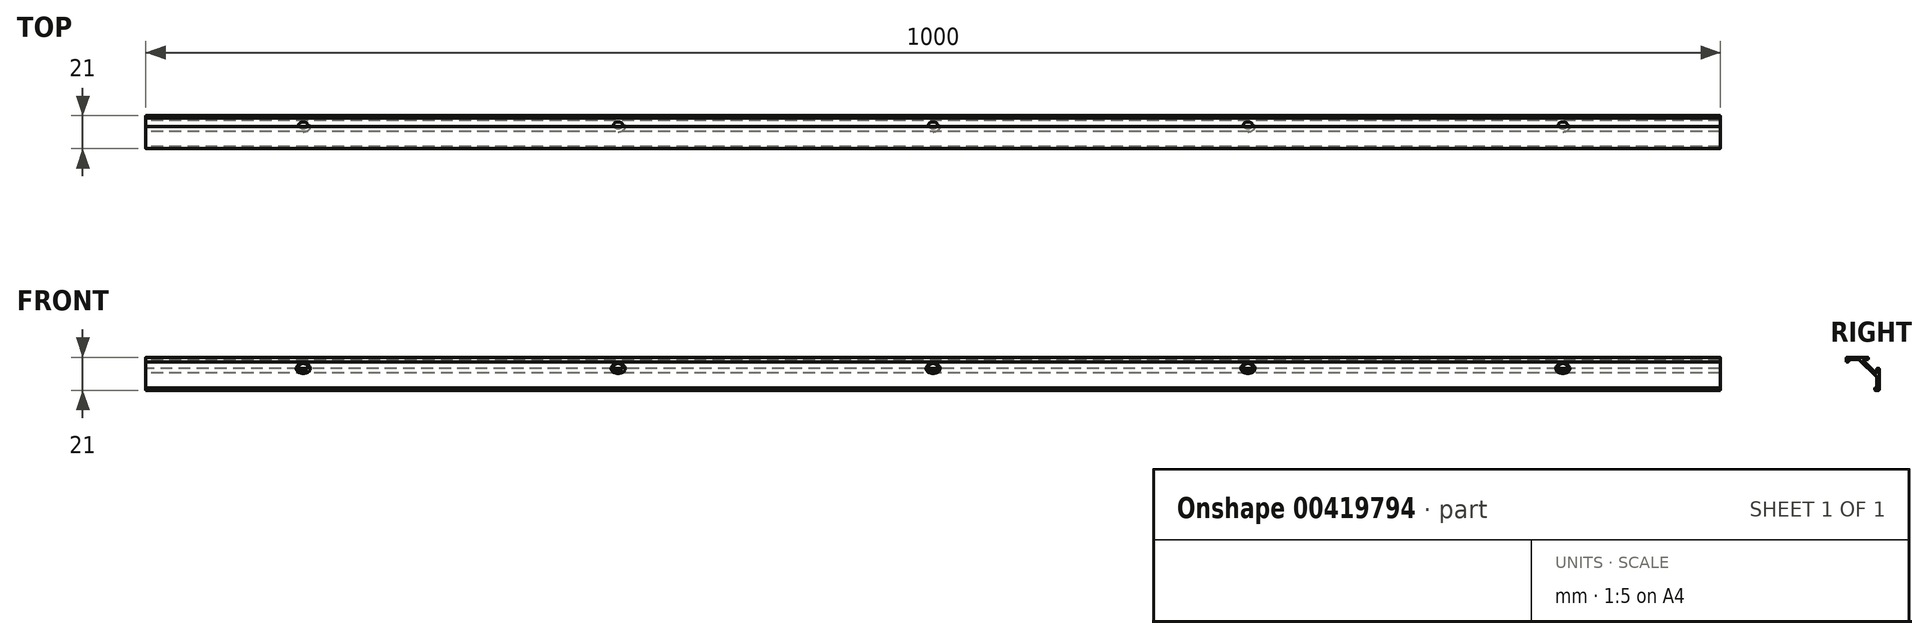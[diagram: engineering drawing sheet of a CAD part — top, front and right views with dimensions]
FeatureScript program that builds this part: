
annotation { "Feature Type Name" : "Feature", "Feature Type Description" : "" }
export const myFeature = defineFeature(function(context is Context, id is Id, definition is map)
    precondition{}
    {
        {
            var Q0;
            Q0=qCreatedBy(makeId("Right.planeOp"),FACE);
            var sketch = newSketch(context, id + "F0", { "sketchPlane" : qUnion([Q0])});
            skLineSegment(sketch, "E0.bottom", {"start": v(10, -10.5) * mm, "end": v(8, -10.5) * mm});
            skLineSegment(sketch, "E0.top", {"start": v(3, 10.5) * mm, "end": v(-10, 10.5) * mm});
            skLineSegment(sketch, "E0.left", {"start": v(10.5, -10) * mm, "end": v(10.5, 3) * mm});
            skLineSegment(sketch, "E0.right", {"start": v(-10.5, 8) * mm, "end": v(-10.5, 10) * mm});
            skPoint(sketch, "E0.middle", {"position": v(0, 0) * mm});
            skLineSegment(sketch, "E1.0", {"start": v(-9, 8) * mm, "end": v(-9, 8.5) * mm});
            skLineSegment(sketch, "E2.0", {"start": v(8.5, -9) * mm, "end": v(8, -9) * mm});
            skLineSegment(sketch, "E3.0", {"start": v(3.5, 9.5) * mm, "end": v(3.5, 10) * mm, "construction": true});
            skLineSegment(sketch, "E4.0", {"start": v(10, 3.5) * mm, "end": v(9.5, 3.5) * mm, "construction": true});
            skLineSegment(sketch, "E5.trimOffspring", {"start": v(-9.5, 7.5) * mm, "end": v(-10, 7.5) * mm});
            skLineSegment(sketch, "E6.0", {"start": v(7.5, -10) * mm, "end": v(7.5, -9.5) * mm});
            skPoint(sketch, "E7.orphan", {"position": v(-10.5, -10.5) * mm});
            skArc(sketch, "E8.filletArc", {"start": v(-8.5, 9) * mm, "mid": v(-8.85, 8.85) * mm, "end": v(-9, 8.5) * mm});
            skArc(sketch, "E9.filletArc", {"start": v(-9.5, 7.5) * mm, "mid": v(-9.15, 7.65) * mm, "end": v(-9, 8) * mm});
            skPoint(sketch, "E10.visualSharp", {"position": v(-10.5, 7.5) * mm});
            skArc(sketch, "E10.filletArc", {"start": v(-10.5, 8) * mm, "mid": v(-10.35, 7.65) * mm, "end": v(-10, 7.5) * mm});
            skArc(sketch, "E11.filletArc", {"start": v(-10, 10.5) * mm, "mid": v(-10.35, 10.35) * mm, "end": v(-10.5, 10) * mm});
            skPoint(sketch, "E12.visualSharp", {"position": v(7.5, -9) * mm});
            skArc(sketch, "E12.filletArc", {"start": v(8, -9) * mm, "mid": v(7.65, -9.15) * mm, "end": v(7.5, -9.5) * mm});
            skPoint(sketch, "E13.visualSharp", {"position": v(7.5, -10.5) * mm});
            skArc(sketch, "E13.filletArc", {"start": v(7.5, -10) * mm, "mid": v(7.65, -10.35) * mm, "end": v(8, -10.5) * mm});
            skPoint(sketch, "E14.visualSharp", {"position": v(10.5, -10.5) * mm});
            skArc(sketch, "E14.filletArc", {"start": v(10, -10.5) * mm, "mid": v(10.35, -10.35) * mm, "end": v(10.5, -10) * mm});
            skArc(sketch, "E15.filletArc", {"start": v(8.5, -9) * mm, "mid": v(8.85, -8.85) * mm, "end": v(9, -8.5) * mm});
            skLineSegment(sketch, "E16.trimOffspring", {"start": v(-2.52, 9) * mm, "end": v(-8.5, 9) * mm});
            skLineSegment(sketch, "E17.trimOffspring", {"start": v(9, -2.52) * mm, "end": v(9, -8.5) * mm});
            skArc(sketch, "E18.filletArc", {"start": v(8.15, 0.66) * mm, "mid": v(8.7, 0.55) * mm, "end": v(9, 1.01) * mm});
            skArc(sketch, "E19.filletArc", {"start": v(1.01, 9) * mm, "mid": v(0.55, 8.7) * mm, "end": v(0.66, 8.15) * mm});
            skArc(sketch, "E20.filletArc", {"start": v(9, -2.52) * mm, "mid": v(8.96, -2.33) * mm, "end": v(8.85, -2.17) * mm});
            skArc(sketch, "E21.filletArc", {"start": v(-2.17, 8.85) * mm, "mid": v(-2.33, 8.96) * mm, "end": v(-2.52, 9) * mm});
            skLineSegment(sketch, "E22", {"start": v(3.5, 10) * mm, "end": v(3.5, 9.5) * mm});
            skLineSegment(sketch, "E23", {"start": v(10, 3.5) * mm, "end": v(9.5, 3.5) * mm});
            skArc(sketch, "E24.filletArc", {"start": v(3, 9) * mm, "mid": v(3.35, 9.15) * mm, "end": v(3.5, 9.5) * mm});
            skArc(sketch, "E25.filletArc", {"start": v(3.5, 10) * mm, "mid": v(3.35, 10.35) * mm, "end": v(3, 10.5) * mm});
            skArc(sketch, "E26.filletArc", {"start": v(9.5, 3.5) * mm, "mid": v(9.15, 3.35) * mm, "end": v(9, 3) * mm});
            skArc(sketch, "E27.filletArc", {"start": v(10.5, 3) * mm, "mid": v(10.35, 3.35) * mm, "end": v(10, 3.5) * mm});
            skLineSegment(sketch, "E28", {"start": v(7.5, -10.5) * mm, "end": v(-10.5, 7.5) * mm, "construction": true});
            skLineSegment(sketch, "E29", {"start": v(0.66, 8.15) * mm, "end": v(8.15, 0.66) * mm});
            skLineSegment(sketch, "E30", {"start": v(8.85, -2.17) * mm, "end": v(-2.17, 8.85) * mm});
            skLineSegment(sketch, "E31", {"start": v(9, 3) * mm, "end": v(9, 1.01) * mm});
            skLineSegment(sketch, "E32", {"start": v(3, 9) * mm, "end": v(1.01, 9) * mm});
            skSolve(sketch);
        }
        {
            var Q0;
            Q0=makeQuery(id+"F0.imprint","IMPRINT",FACE,{"disambiguationData":[TD([[makeQuery(id+"F0.imprint","IMPRINT",EDGE,{"derivedFrom":sQuery(id+"F0.wireOp",EDGE,"E0.bottom")}),-1.0]])]});
            extrude(context, id + "F1", {"entities" : qUnion([Q0]), "depth" : 1000 * mm});
        }
        {
            var Q0;
            Q0=makeQuery(id+"F1.opExtrude","SWEPT_FACE",FACE,{"disambiguationData":[OSD([sQuery(id+"F0.wireOp",EDGE,"E30")])]});
            var sketch = newSketch(context, id + "F2", { "sketchPlane" : qUnion([Q0])});
            skLineSegment(sketch, "E33", {"start": v(0, 0) * mm, "end": v(250, 0) * mm});
            skLineSegment(sketch, "E34.0", {"start": v(900, 4.8) * mm, "end": v(900, -4.8) * mm, "construction": true});
            skLineSegment(sketch, "E35.0", {"start": v(700, 4.8) * mm, "end": v(700, -4.8) * mm, "construction": true});
            skLineSegment(sketch, "E36.0", {"start": v(500, 4.8) * mm, "end": v(500, -4.8) * mm, "construction": true});
            skLineSegment(sketch, "E37.0", {"start": v(300, 4.8) * mm, "end": v(300, -4.8) * mm, "construction": true});
            skPoint(sketch, "E38", {"position": v(300, 0) * mm});
            skPoint(sketch, "E39", {"position": v(500, 0) * mm});
            skPoint(sketch, "E40", {"position": v(700, 0) * mm});
            skPoint(sketch, "E41", {"position": v(900, 0) * mm});
            skLineSegment(sketch, "E42.0", {"start": v(100, 4.8) * mm, "end": v(100, -4.8) * mm});
            skPoint(sketch, "E43", {"position": v(100, 0) * mm});
            skSolve(sketch);
        }
        {
            var Q0;
            Q0=sQuery(id+"F2.wireOp",VERTEX,"E38");
            var Q1;
            Q1=sQuery(id+"F2.wireOp",VERTEX,"E39");
            var Q2;
            Q2=sQuery(id+"F2.wireOp",VERTEX,"E40");
            var Q3;
            Q3=sQuery(id+"F2.wireOp",VERTEX,"E41");
            var Q4;
            Q4=sQuery(id+"F2.wireOp",VERTEX,"E43");
            var Q5;
            Q5=makeQuery(id+"F1.opExtrude","SWEPT_BODY",BODY,{"disambiguationData":[OSD([sQuery(id+"F0.wireOp",EDGE,"E0.bottom"),sQuery(id+"F0.wireOp",EDGE,"E0.top"),sQuery(id+"F0.wireOp",EDGE,"E0.left"),sQuery(id+"F0.wireOp",EDGE,"E0.right"),sQuery(id+"F0.wireOp",EDGE,"E1.0"),sQuery(id+"F0.wireOp",EDGE,"E2.0"),sQuery(id+"F0.wireOp",EDGE,"s1j5iu09-LJZy-9apo-odkQ-GbOXyxKkjL7w"),sQuery(id+"F0.wireOp",EDGE,"fCwWEJ1m-8jWg-r8aV-jBB4-E1VlMGMAYnd8"),sQuery(id+"F0.wireOp",EDGE,"dBWzYiSR-O6vT-lZNa-yt61-WvQArz2e6oIL"),sQuery(id+"F0.wireOp",EDGE,"5646912a-2fe8-4067-a2b1-a6853a4d93ac.trimOffspring"),sQuery(id+"F0.wireOp",EDGE,"90c1620c-5f87-4e04-bfff-8c39e82e8872.filletArc"),sQuery(id+"F0.wireOp",EDGE,"3f26777e-f9e8-4980-8723-1eca19a36066.filletArc"),sQuery(id+"F0.wireOp",EDGE,"88262fec-1386-4cce-bb0b-ab2af3b31e36.filletArc"),sQuery(id+"F0.wireOp",EDGE,"128d30bb-c364-4ff7-9227-d5dd6045fd1c.filletArc"),sQuery(id+"F0.wireOp",EDGE,"b2f7425b-e175-4acd-bc16-6d01453e2797.filletArc"),sQuery(id+"F0.wireOp",EDGE,"c13f3c6c-cf2c-4a04-8761-6f3bb6855f8a.filletArc"),sQuery(id+"F0.wireOp",EDGE,"8FEjWMV3-qNy8-Z6mM-26rj-OPhPC0TwsFZj"),sQuery(id+"F0.wireOp",EDGE,"OAoDRjdF-DLSa-YlZY-3xl2-rc9FAVTqj5e3"),sQuery(id+"F0.wireOp",EDGE,"E5.trimOffspring"),sQuery(id+"F0.wireOp",EDGE,"E6.0"),sQuery(id+"F0.wireOp",EDGE,"E8.filletArc"),sQuery(id+"F0.wireOp",EDGE,"E9.filletArc"),sQuery(id+"F0.wireOp",EDGE,"E10.filletArc"),sQuery(id+"F0.wireOp",EDGE,"E11.filletArc"),sQuery(id+"F0.wireOp",EDGE,"E12.filletArc"),sQuery(id+"F0.wireOp",EDGE,"E13.filletArc"),sQuery(id+"F0.wireOp",EDGE,"E14.filletArc"),sQuery(id+"F0.wireOp",EDGE,"E15.filletArc"),sQuery(id+"F0.wireOp",EDGE,"9374389a-d2e3-4b9a-a025-4b08a2ce4334.trimOffspring"),sQuery(id+"F0.wireOp",EDGE,"39bb24a7-ac00-4b4d-bd90-0e8144d3d5aa.trimOffspring"),sQuery(id+"F0.wireOp",EDGE,"04bc3d8c-4601-4e91-9dbe-31d66d5429b3.filletArc"),sQuery(id+"F0.wireOp",EDGE,"acb3b3da-af41-4877-a126-f793060302c6.filletArc")])]});
            hole(context, id + "F3", {"style" : HoleStyle.C_SINK, "endStyle" : HoleEndStyle.THROUGH, "standardTappedOrClearance" : lookupTablePath({ "standard" : "ISO", "fit" : "Normal", "size" : "M4", "type" : "Clearance" }), "standardBlindInLast" : lookupTablePath({ "fit" : "Standard", "standard" : "ISO", "size" : "M4", "type" : "Clearance" }), "holeDiameter" : 4.4 * mm, "cSinkDiameter" : 8.96 * mm, "cSinkAngle" : 90 * degree, "isTappedThrough" : true, "tappedDepth" : 12 * mm, "tapClearance" : 3, "locations" : qUnion([Q0, Q1, Q2, Q3, Q4]), "scope" : qUnion([Q5]), "startStyle" : HoleStartStyle.PART});
        }
    });
